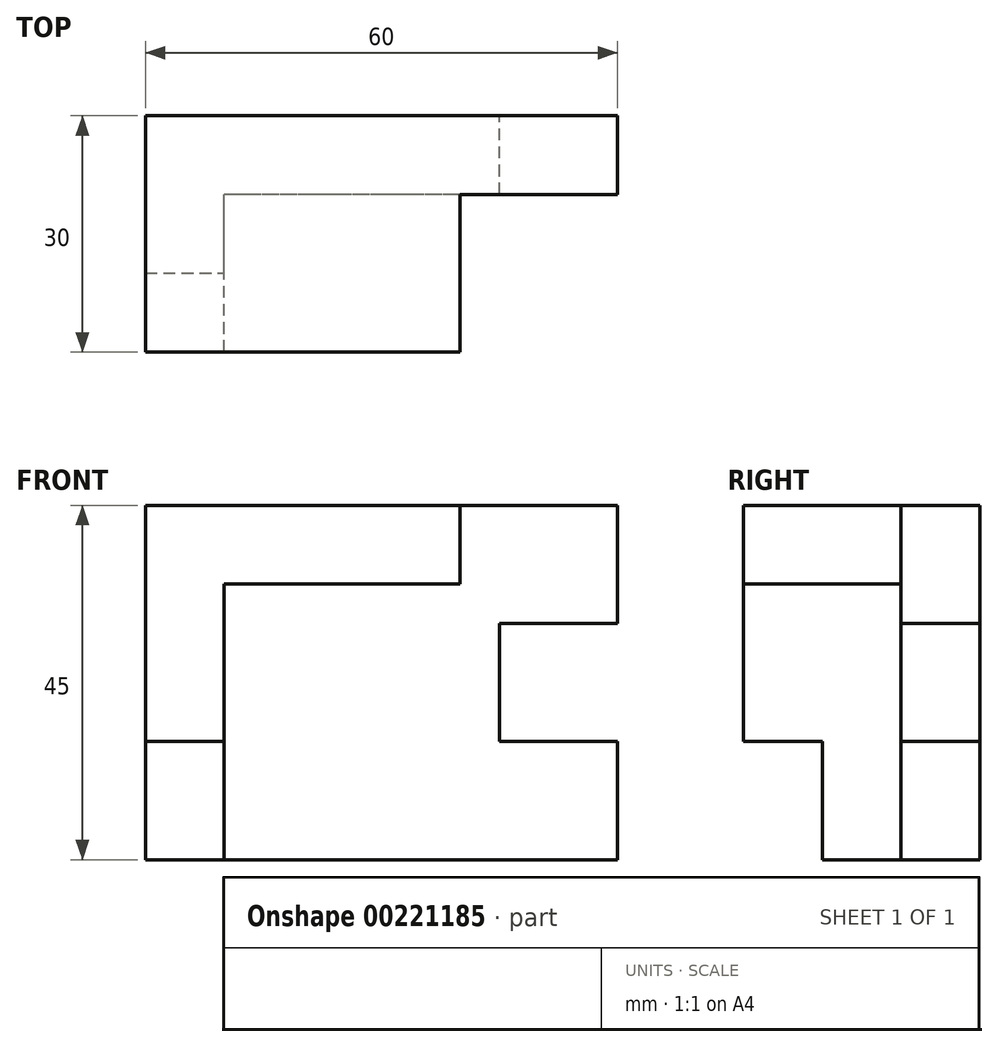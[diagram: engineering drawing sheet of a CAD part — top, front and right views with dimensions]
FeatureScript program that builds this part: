
annotation { "Feature Type Name" : "Feature", "Feature Type Description" : "" }
export const myFeature = defineFeature(function(context is Context, id is Id, definition is map)
    precondition{}
    {
        {
            var Q0;
            Q0=qCreatedBy(makeId("Front.planeOp"),FACE);
            var sketch = newSketch(context, id + "F0", { "sketchPlane" : qUnion([Q0])});
            skLineSegment(sketch, "E0", {"start": v(0, 0) * mm, "end": v(0, 15) * mm});
            skLineSegment(sketch, "E1", {"start": v(0, 15) * mm, "end": v(10, 15) * mm});
            skLineSegment(sketch, "E2", {"start": v(10, 15) * mm, "end": v(10, 0) * mm});
            skLineSegment(sketch, "E3", {"start": v(10, 0) * mm, "end": v(0, 0) * mm});
            skLineSegment(sketch, "E4", {"start": v(0, 15) * mm, "end": v(0, 45) * mm});
            skLineSegment(sketch, "E5", {"start": v(0, 45) * mm, "end": v(40, 45) * mm});
            skLineSegment(sketch, "E6", {"start": v(40, 45) * mm, "end": v(40, 35) * mm});
            skLineSegment(sketch, "E7", {"start": v(40, 35) * mm, "end": v(10, 35) * mm});
            skLineSegment(sketch, "E8", {"start": v(10, 35) * mm, "end": v(10, 15) * mm});
            skLineSegment(sketch, "E9", {"start": v(40, 45) * mm, "end": v(60, 45) * mm});
            skLineSegment(sketch, "E10", {"start": v(60, 45) * mm, "end": v(60, 30) * mm});
            skLineSegment(sketch, "E11", {"start": v(60, 30) * mm, "end": v(45, 30) * mm});
            skLineSegment(sketch, "E12", {"start": v(45, 30) * mm, "end": v(45, 15) * mm});
            skLineSegment(sketch, "E13", {"start": v(45, 15) * mm, "end": v(60, 15) * mm});
            skLineSegment(sketch, "E14", {"start": v(60, 15) * mm, "end": v(60, 0) * mm});
            skLineSegment(sketch, "E15", {"start": v(60, 0) * mm, "end": v(10, 0) * mm});
            skSolve(sketch);
        }
        {
            var Q0;
            Q0=makeQuery(id+"F0.imprint","IMPRINT",FACE,{"disambiguationData":[TD([[makeQuery(id+"F0.imprint","IMPRINT",EDGE,{"derivedFrom":sQuery(id+"F0.wireOp",EDGE,"E1")}),1.0]])]});
            extrude(context, id + "F1", {"entities" : qUnion([Q0]), "depth" : 30 * mm});
        }
        {
            var Q0;
            Q0=makeQuery(id+"F0.imprint","IMPRINT",FACE,{"disambiguationData":[TD([[makeQuery(id+"F0.imprint","IMPRINT",EDGE,{"derivedFrom":sQuery(id+"F0.wireOp",EDGE,"E2")}),1.0]])]});
            extrude(context, id + "F2", {"entities" : qUnion([Q0]), "operationType" : NewBodyOperationType.ADD, "depth" : 10 * mm});
        }
        {
            var Q0;
            Q0=makeQuery(id+"F0.imprint","IMPRINT",FACE,{"disambiguationData":[TD([[makeQuery(id+"F0.imprint","IMPRINT",EDGE,{"derivedFrom":sQuery(id+"F0.wireOp",EDGE,"E0")}),-1.0]])]});
            extrude(context, id + "F3", {"entities" : qUnion([Q0]), "operationType" : NewBodyOperationType.ADD, "depth" : 20 * mm});
        }
    });
